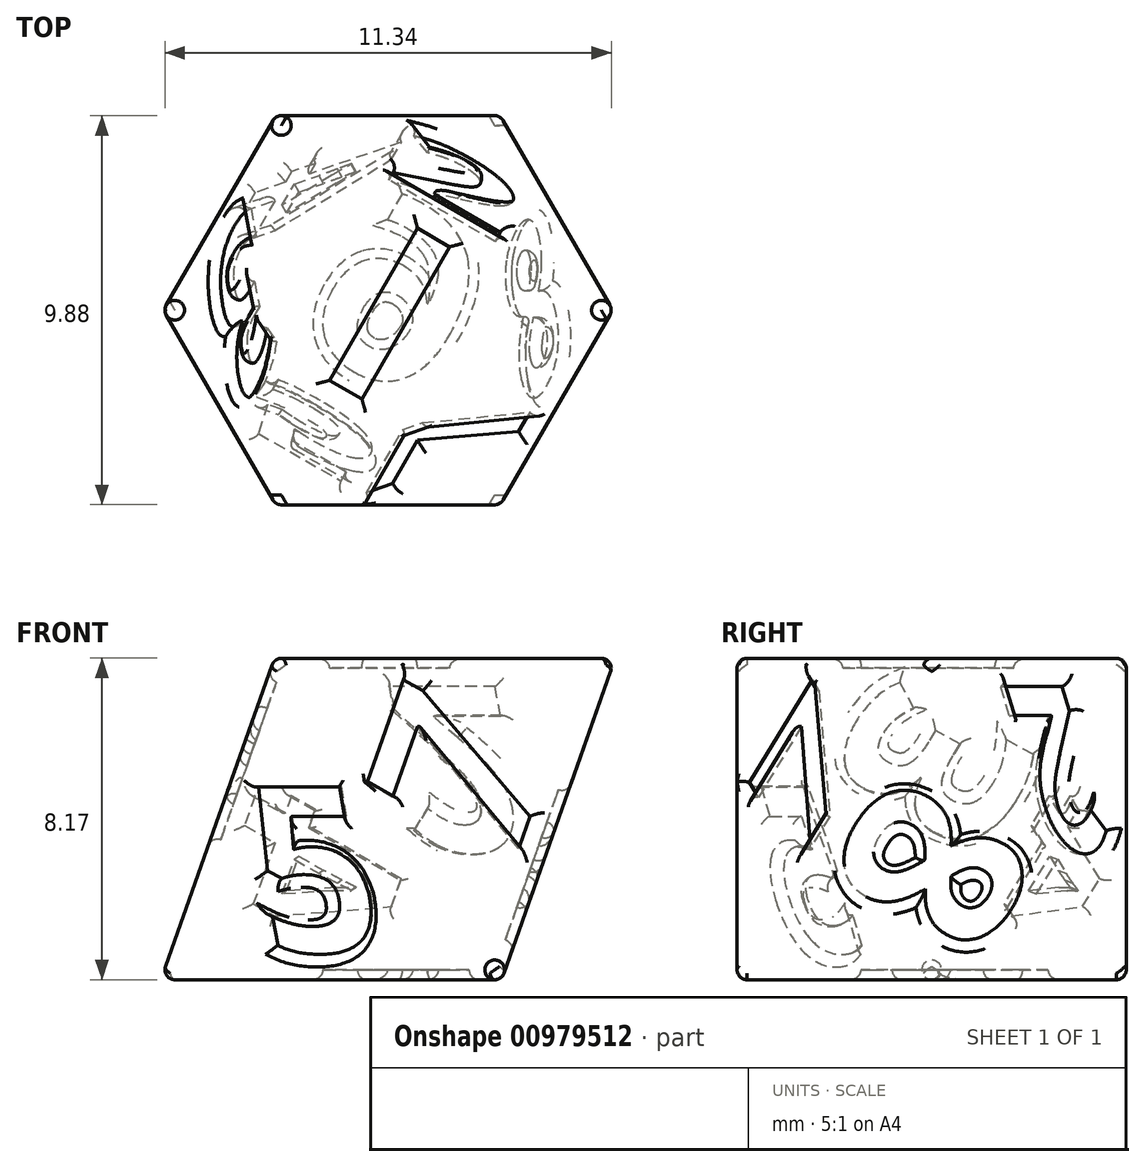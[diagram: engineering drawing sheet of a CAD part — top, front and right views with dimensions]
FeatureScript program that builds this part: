
annotation { "Feature Type Name" : "Feature", "Feature Type Description" : "" }
export const myFeature = defineFeature(function(context is Context, id is Id, definition is map)
    precondition{}
    {
        {
            var Q0;
            Q0=qCreatedBy(makeId("Top.planeOp"),FACE);
            var sketch = newSketch(context, id + "F0", { "sketchPlane" : qUnion([Q0])});
            skCircle(sketch, "E0.cCircle", {"center": v(0, 0) * mm, "radius": 2.89 * mm, "construction": true});
            skLineSegment(sketch, "E0.0", {"start": v(2.89, 5) * mm, "end": v(2.89, -5) * mm});
            skLineSegment(sketch, "E0.1", {"start": v(2.89, -5) * mm, "end": v(-5.77, 0) * mm});
            skLineSegment(sketch, "E0.2", {"start": v(-5.77, 0) * mm, "end": v(2.89, 5) * mm});
            skPoint(sketch, "E0.0.midPoint", {"position": v(2.89, 0) * mm});
            skSolve(sketch);
        }
        {
            var Q0;
            Q0=sQuery(id+"F0.wireOp",EDGE,"E0.2");
            cPlane(context, id + "F1", {"entities" : qUnion([Q0]), "cplaneType" : CPlaneType.LINE_ANGLE, "offset" : 25 * mm, "angle" : 199.47 * degree, "oppositeDirection" : true, "width" : 150 * mm, "height" : 150 * mm});
        }
        {
            var Q0;
            Q0=qCreatedBy(id+"F1.planeOp",FACE);
            var sketch = newSketch(context, id + "F2", { "sketchPlane" : qUnion([Q0])});
            skCircle(sketch, "E1.cCircle", {"center": v(-0.73, 3.78) * mm, "radius": 2.89 * mm, "construction": true});
            skLineSegment(sketch, "E1.0", {"start": v(4.73, 1.89) * mm, "end": v(-5.1, 0) * mm});
            skLineSegment(sketch, "E1.1", {"start": v(-5.1, 0) * mm, "end": v(-1.82, 9.45) * mm});
            skLineSegment(sketch, "E1.2", {"start": v(-1.82, 9.45) * mm, "end": v(4.73, 1.89) * mm});
            skPoint(sketch, "E1.0.midPoint", {"position": v(-0.18, 0.94) * mm});
            skSolve(sketch);
        }
        {
            var Q0;
            Q0=sQuery(id+"F0.wireOp",EDGE,"E0.0");
            cPlane(context, id + "F3", {"entities" : qUnion([Q0]), "cplaneType" : CPlaneType.LINE_ANGLE, "offset" : 25 * mm, "angle" : 109.47 * degree, "oppositeDirection" : true, "width" : 150 * mm, "height" : 150 * mm});
        }
        {
            var Q0;
            Q0=qCreatedBy(id+"F3.planeOp",FACE);
            var sketch = newSketch(context, id + "F4", { "sketchPlane" : qUnion([Q0])});
            skCircle(sketch, "E2.cCircle", {"center": v(0, 3.85) * mm, "radius": 2.89 * mm, "construction": true});
            skLineSegment(sketch, "E2.0", {"start": v(5, 0.96) * mm, "end": v(-5, 0.96) * mm});
            skLineSegment(sketch, "E2.1", {"start": v(-5, 0.96) * mm, "end": v(0, 9.62) * mm});
            skLineSegment(sketch, "E2.2", {"start": v(0, 9.62) * mm, "end": v(5, 0.96) * mm});
            skPoint(sketch, "E2.0.midPoint", {"position": v(0, 0.96) * mm});
            skSolve(sketch);
        }
        {
            var Q0;
            Q0=sQuery(id+"F0.wireOp",VERTEX,"E0.0.start");
            var Q1;
            Q1=sQuery(id+"F2.wireOp",VERTEX,"E1.1.end");
            var Q2;
            Q2=sQuery(id+"F4.wireOp",VERTEX,"E2.1.end");
            cPlane(context, id + "F5", {"entities" : qUnion([Q0, Q1, Q2]), "cplaneType" : CPlaneType.THREE_POINT, "offset" : 25 * mm, "width" : 150 * mm, "height" : 150 * mm});
        }
        {
            var Q0;
            Q0=qCreatedBy(id+"F5.planeOp",FACE);
            var sketch = newSketch(context, id + "F6", { "sketchPlane" : qUnion([Q0])});
            skPoint(sketch, "E3.0", {"position": v(3.64, 7.56) * mm});
            skPoint(sketch, "E4.0", {"position": v(-6.18, 5.67) * mm});
            skLineSegment(sketch, "E5", {"start": v(3.64, 7.56) * mm, "end": v(-6.18, 5.67) * mm});
            skPoint(sketch, "E6.0", {"position": v(0.36, -1.89) * mm});
            skLineSegment(sketch, "E7", {"start": v(3.64, 7.56) * mm, "end": v(0.36, -1.89) * mm});
            skLineSegment(sketch, "E8", {"start": v(-6.18, 5.67) * mm, "end": v(0.36, -1.89) * mm});
            skSolve(sketch);
        }
        {
            var Q0;
            Q0=sQuery(id+"F0.wireOp",EDGE,"E0.1");
            cPlane(context, id + "F7", {"entities" : qUnion([Q0]), "cplaneType" : CPlaneType.LINE_ANGLE, "offset" : 25 * mm, "angle" : 199.47 * degree, "oppositeDirection" : true, "width" : 150 * mm, "height" : 150 * mm});
        }
        {
            var Q0;
            Q0=qCreatedBy(id+"F7.planeOp",FACE);
            var sketch = newSketch(context, id + "F8", { "sketchPlane" : qUnion([Q0])});
            skCircle(sketch, "E9.cCircle", {"center": v(0.73, 3.78) * mm, "radius": 2.89 * mm, "construction": true});
            skLineSegment(sketch, "E9.0", {"start": v(5.1, 0) * mm, "end": v(-4.73, 1.89) * mm});
            skLineSegment(sketch, "E9.1", {"start": v(-4.73, 1.89) * mm, "end": v(1.82, 9.45) * mm});
            skLineSegment(sketch, "E9.2", {"start": v(1.82, 9.45) * mm, "end": v(5.1, 0) * mm});
            skPoint(sketch, "E9.0.midPoint", {"position": v(0.18, 0.94) * mm});
            skSolve(sketch);
        }
        {
            var Q0;
            Q0=sQuery(id+"F6.wireOp",VERTEX,"E4.0");
            var Q1;
            Q1=sQuery(id+"F8.wireOp",VERTEX,"E9.1.end");
            var Q2;
            Q2=sQuery(id+"F6.wireOp",VERTEX,"E3.0");
            cPlane(context, id + "F9", {"entities" : qUnion([Q0, Q1, Q2]), "cplaneType" : CPlaneType.THREE_POINT, "offset" : 25 * mm, "width" : 150 * mm, "height" : 150 * mm});
        }
        {
            var Q0;
            Q0=qCreatedBy(id+"F9.planeOp",FACE);
            var sketch = newSketch(context, id + "F10", { "sketchPlane" : qUnion([Q0])});
            skCircle(sketch, "E10.cCircle", {"center": v(0, 0) * mm, "radius": 2.89 * mm, "construction": true});
            skLineSegment(sketch, "E10.0", {"start": v(5.77, 0) * mm, "end": v(-2.89, -5) * mm});
            skLineSegment(sketch, "E10.1", {"start": v(-2.89, -5) * mm, "end": v(-2.89, 5) * mm});
            skLineSegment(sketch, "E10.2", {"start": v(-2.89, 5) * mm, "end": v(5.77, 0) * mm});
            skPoint(sketch, "E10.0.midPoint", {"position": v(1.44, -2.5) * mm});
            skSolve(sketch);
        }
        {
            var Q0;
            Q0=sQuery(id+"F6.wireOp",VERTEX,"E4.0");
            var Q1;
            Q1=sQuery(id+"F0.wireOp",VERTEX,"E0.1.end");
            var Q2;
            Q2=sQuery(id+"F8.wireOp",VERTEX,"E9.1.end");
            cPlane(context, id + "F11", {"entities" : qUnion([Q0, Q1, Q2]), "cplaneType" : CPlaneType.THREE_POINT, "offset" : 25 * mm, "width" : 150 * mm, "height" : 150 * mm});
        }
        {
            var Q0;
            Q0=qCreatedBy(id+"F11.planeOp",FACE);
            var sketch = newSketch(context, id + "F12", { "sketchPlane" : qUnion([Q0])});
            skCircle(sketch, "E11.cCircle", {"center": v(0, 3.85) * mm, "radius": 2.89 * mm, "construction": true});
            skLineSegment(sketch, "E11.0", {"start": v(0, -1.92) * mm, "end": v(-5, 6.74) * mm});
            skLineSegment(sketch, "E11.1", {"start": v(-5, 6.74) * mm, "end": v(5, 6.74) * mm});
            skLineSegment(sketch, "E11.2", {"start": v(5, 6.74) * mm, "end": v(0, -1.92) * mm});
            skPoint(sketch, "E11.0.midPoint", {"position": v(-2.5, 2.4) * mm});
            skSolve(sketch);
        }
        {
            var Q0;
            Q0=sQuery(id+"F0.wireOp",VERTEX,"E0.0.end");
            var Q1;
            Q1=sQuery(id+"F8.wireOp",VERTEX,"E9.1.end");
            var Q2;
            Q2=sQuery(id+"F6.wireOp",VERTEX,"E3.0");
            cPlane(context, id + "F13", {"entities" : qUnion([Q0, Q1, Q2]), "cplaneType" : CPlaneType.THREE_POINT, "offset" : 25 * mm, "width" : 150 * mm, "height" : 150 * mm});
        }
        {
            var Q0;
            Q0=qCreatedBy(id+"F13.planeOp",FACE);
            var sketch = newSketch(context, id + "F14", { "sketchPlane" : qUnion([Q0])});
            skCircle(sketch, "E12.cCircle", {"center": v(-0.73, 3.78) * mm, "radius": 2.89 * mm, "construction": true});
            skLineSegment(sketch, "E12.0", {"start": v(3.64, 7.56) * mm, "end": v(0.36, -1.89) * mm});
            skLineSegment(sketch, "E12.1", {"start": v(0.36, -1.89) * mm, "end": v(-6.18, 5.67) * mm});
            skLineSegment(sketch, "E12.2", {"start": v(-6.18, 5.67) * mm, "end": v(3.64, 7.56) * mm});
            skPoint(sketch, "E12.0.midPoint", {"position": v(2, 2.83) * mm});
            skSolve(sketch);
        }
        {
            var Q0;
            Q0=makeQuery(id+"F6.imprint","IMPRINT",FACE,{"disambiguationData":[TD([[makeQuery(id+"F6.imprint","IMPRINT",EDGE,{"derivedFrom":sQuery(id+"F6.wireOp",EDGE,"E5")}),1.0]])]});
            var Q1;
            Q1=makeQuery(id+"F8.imprint","IMPRINT",FACE,{"disambiguationData":[TD([[makeQuery(id+"F8.imprint","IMPRINT",EDGE,{"derivedFrom":sQuery(id+"F8.wireOp",EDGE,"E9.0")}),-1.0]])]});
            loft(context, id + "F15", {"sheetProfilesArray" : [{ "sheetProfileEntities" : qUnion([Q0]) }, { "sheetProfileEntities" : qUnion([Q1]) }]});
        }
        {
            var Q1;
            Q1=makeQuery(id+"F2.imprint","IMPRINT",FACE,{"disambiguationData":[TD([[makeQuery(id+"F2.imprint","IMPRINT",EDGE,{"derivedFrom":sQuery(id+"F2.wireOp",EDGE,"E1.0")}),-1.0]])]});
            var Q2;
            Q2=makeQuery(id+"F14.imprint","IMPRINT",FACE,{"disambiguationData":[TD([[makeQuery(id+"F14.imprint","IMPRINT",EDGE,{"derivedFrom":sQuery(id+"F14.wireOp",EDGE,"E12.0")}),-1.0]])]});
            loft(context, id + "F16", {"operationType" : NewBodyOperationType.ADD, "sheetProfilesArray" : [{ "sheetProfileEntities" : qUnion([Q1]) }, { "sheetProfileEntities" : qUnion([Q2]) }]});
        }
        {
            var Q1;
            Q1=makeQuery(id+"F10.imprint","IMPRINT",FACE,{"disambiguationData":[TD([[makeQuery(id+"F10.imprint","IMPRINT",EDGE,{"derivedFrom":sQuery(id+"F10.wireOp",EDGE,"E10.0")}),-1.0]])]});
            var Q2;
            Q2=makeQuery(id+"F0.imprint","IMPRINT",FACE,{"disambiguationData":[TD([[makeQuery(id+"F0.imprint","IMPRINT",EDGE,{"derivedFrom":sQuery(id+"F0.wireOp",EDGE,"E0.0")}),-1.0]])]});
            loft(context, id + "F17", {"operationType" : NewBodyOperationType.ADD, "sheetProfilesArray" : [{ "sheetProfileEntities" : qUnion([Q1]) }, { "sheetProfileEntities" : qUnion([Q2]) }]});
        }
        {
            var Q1;
            Q1=makeQuery(id+"F12.imprint","IMPRINT",FACE,{"disambiguationData":[TD([[makeQuery(id+"F12.imprint","IMPRINT",EDGE,{"derivedFrom":sQuery(id+"F12.wireOp",EDGE,"E11.0")}),-1.0]])]});
            var Q2;
            Q2=makeQuery(id+"F4.imprint","IMPRINT",FACE,{"disambiguationData":[TD([[makeQuery(id+"F4.imprint","IMPRINT",EDGE,{"derivedFrom":sQuery(id+"F4.wireOp",EDGE,"E2.0")}),-1.0]])]});
            loft(context, id + "F18", {"operationType" : NewBodyOperationType.ADD, "sheetProfilesArray" : [{ "sheetProfileEntities" : qUnion([Q1]) }, { "sheetProfileEntities" : qUnion([Q2]) }]});
        }
        {
            var Q0;
            Q0=makeQuery(id+"F17.opLoft","CAP_FACE",FACE,{"disambiguationData":[OSD([makeQuery(id+"F10.imprint","IMPRINT",FACE,{"disambiguationData":[TD([[makeQuery(id+"F10.imprint","IMPRINT",EDGE,{"derivedFrom":sQuery(id+"F10.wireOp",EDGE,"E10.0")}),-1.0]])]})])],"isStart":true});
            var sketch = newSketch(context, id + "F19", { "sketchPlane" : qUnion([Q0])});
            skText(sketch, "E13", { "text": "I", "fontName": "OpenSans-Bold.ttf"});
            skLineSegment(sketch, "E14", {"start": v(-2.89, -5) * mm, "end": v(-1.14, -1.97) * mm, "construction": true});
            const initialGuessF19  = {"E13": [-0.00197, -0.0015, 0.86603, -0.5, 0.0045]};
            skSetInitialGuess(sketch, initialGuessF19);
            skSolve(sketch);
        }
        {
            var Q0;
            Q0=makeQuery(id+"F19.imprint","IMPRINT",FACE,{"disambiguationData":[TD([[makeQuery(id+"F19.imprint","IMPRINT",EDGE,{"derivedFrom":sQuery(id+"F19.wireOp",EDGE,"E13.sketch_text.stroke-0")}),-1.0]])]});
            extrude(context, id + "F20", {"entities" : qUnion([Q0]), "operationType" : NewBodyOperationType.REMOVE, "oppositeDirection" : true, "depth" : .25 * mm, "offsetDistance" : 25 * mm});
        }
        {
            var Q0;
            Q0=makeQuery(id+"F18.opLoft","CAP_FACE",FACE,{"disambiguationData":[OSD([makeQuery(id+"F12.imprint","IMPRINT",FACE,{"disambiguationData":[TD([[makeQuery(id+"F12.imprint","IMPRINT",EDGE,{"derivedFrom":sQuery(id+"F12.wireOp",EDGE,"E11.0")}),-1.0]])]})])],"isStart":true});
            var sketch = newSketch(context, id + "F21", { "sketchPlane" : qUnion([Q0])});
            skText(sketch, "E15", { "text": "3", "fontName": "OpenSans-Bold.ttf"});
            skLineSegment(sketch, "E16", {"start": v(5, 6.74) * mm, "end": v(1.97, 4.99) * mm, "construction": true});
            skPoint(sketch, "E17.0", {"position": v(-2.5, 2.4) * mm});
            skLineSegment(sketch, "E18", {"start": v(-2.5, 2.4) * mm, "end": v(-1.93, 2.74) * mm, "construction": true});
            skFitSpline(sketch, "E19.0", {"points": [v(-5, 6.74) * mm, v(0, -1.92) * mm]});
            const initialGuessF21  = {"E15": [-0.00286, 0.00435, 0.49999, -0.86603, 0.0045]};
            skSetInitialGuess(sketch, initialGuessF21);
            skSolve(sketch);
        }
        {
            var Q0;
            Q0=makeQuery(id+"F21.imprint","IMPRINT",FACE,{"disambiguationData":[TD([[makeQuery(id+"F21.imprint","IMPRINT",EDGE,{"derivedFrom":sQuery(id+"F21.wireOp",EDGE,"E15.sketch_text.stroke-0")}),-1.0]])]});
            extrude(context, id + "F22", {"entities" : qUnion([Q0]), "operationType" : NewBodyOperationType.REMOVE, "oppositeDirection" : true, "depth" : .25 * mm, "offsetDistance" : 25 * mm});
        }
        {
            var Q0;
            Q0=makeQuery(id+"F15.opLoft","CAP_FACE",FACE,{"disambiguationData":[OSD([makeQuery(id+"F8.imprint","IMPRINT",FACE,{"disambiguationData":[TD([[makeQuery(id+"F8.imprint","IMPRINT",EDGE,{"derivedFrom":sQuery(id+"F8.wireOp",EDGE,"E9.0")}),-1.0]])]})])],"isStart":true});
            var sketch = newSketch(context, id + "F23", { "sketchPlane" : qUnion([Q0])});
            skLineSegment(sketch, "E20", {"start": v(-0.18, 0.94) * mm, "end": v(-0.3, 1.6) * mm, "construction": true});
            skLineSegment(sketch, "E21", {"start": v(-1.82, 9.45) * mm, "end": v(-1.16, 6.01) * mm, "construction": true});
            skText(sketch, "E22", { "text": "5", "fontName": "OpenSans-Bold.ttf"});
            const initialGuessF23  = {"E22": [-0.00212, 0.00124, 0.98198, 0.18897, 0.0045]};
            skSetInitialGuess(sketch, initialGuessF23);
            skSolve(sketch);
        }
        {
            var Q0;
            Q0=makeQuery(id+"F23.imprint","IMPRINT",FACE,{"disambiguationData":[TD([[makeQuery(id+"F23.imprint","IMPRINT",EDGE,{"derivedFrom":sQuery(id+"F23.wireOp",EDGE,"E22.sketch_text.stroke-0")}),-1.0]])]});
            extrude(context, id + "F24", {"entities" : qUnion([Q0]), "operationType" : NewBodyOperationType.REMOVE, "oppositeDirection" : true, "depth" : .25 * mm, "offsetDistance" : 25 * mm});
        }
        {
            var Q0;
            Q0=makeQuery(id+"F16.opLoft","CAP_FACE",FACE,{"disambiguationData":[OSD([makeQuery(id+"F14.imprint","IMPRINT",FACE,{"disambiguationData":[TD([[makeQuery(id+"F14.imprint","IMPRINT",EDGE,{"derivedFrom":sQuery(id+"F14.wireOp",EDGE,"E12.0")}),-1.0]])]})])],"isStart":true});
            var sketch = newSketch(context, id + "F25", { "sketchPlane" : qUnion([Q0])});
            skLineSegment(sketch, "E23", {"start": v(2, 2.83) * mm, "end": v(1.38, 3.05) * mm, "construction": true});
            skLineSegment(sketch, "E24", {"start": v(-6.18, 5.67) * mm, "end": v(-2.88, 4.52) * mm, "construction": true});
            skText(sketch, "E25", { "text": "7", "fontName": "OpenSans-Bold.ttf"});
            const initialGuessF25  = {"E25": [0.00076, 0.00127, 0.32732, 0.94491, 0.0045]};
            skSetInitialGuess(sketch, initialGuessF25);
            skSolve(sketch);
        }
        {
            var Q0;
            Q0=makeQuery(id+"F25.imprint","IMPRINT",FACE,{"disambiguationData":[TD([[makeQuery(id+"F25.imprint","IMPRINT",EDGE,{"derivedFrom":sQuery(id+"F25.wireOp",EDGE,"E25.sketch_text.stroke-0")}),-1.0]])]});
            extrude(context, id + "F26", {"entities" : qUnion([Q0]), "operationType" : NewBodyOperationType.REMOVE, "oppositeDirection" : true, "depth" : .25 * mm, "offsetDistance" : 25 * mm});
        }
        {
            var Q0;
            Q0=makeQuery(id+"F17.opLoft","CAP_FACE",FACE,{"disambiguationData":[OSD([makeQuery(id+"F0.imprint","IMPRINT",FACE,{"disambiguationData":[TD([[makeQuery(id+"F0.imprint","IMPRINT",EDGE,{"derivedFrom":sQuery(id+"F0.wireOp",EDGE,"E0.0")}),-1.0]])]})])],"isStart":true});
            var sketch = newSketch(context, id + "F27", { "sketchPlane" : qUnion([Q0])});
            skLineSegment(sketch, "E26", {"start": v(-1.44, 2.5) * mm, "end": v(-0.86, 1.5) * mm, "construction": true});
            skLineSegment(sketch, "E27", {"start": v(2.89, -5) * mm, "end": v(1.39, -2.4) * mm, "construction": true});
            skText(sketch, "E28", { "text": "6", "fontName": "OpenSans-Bold.ttf"});
            const initialGuessF27  = {"E28": [0.00077, 0.00244, -0.86603, -0.5, 0.0045]};
            skSetInitialGuess(sketch, initialGuessF27);
            skSolve(sketch);
        }
        {
            var Q0;
            Q0=makeQuery(id+"F27.imprint","IMPRINT",FACE,{"disambiguationData":[TD([[makeQuery(id+"F27.imprint","IMPRINT",EDGE,{"derivedFrom":sQuery(id+"F27.wireOp",EDGE,"E28.sketch_text.stroke-0")}),-1.0]])]});
            extrude(context, id + "F28", {"entities" : qUnion([Q0]), "operationType" : NewBodyOperationType.REMOVE, "oppositeDirection" : true, "depth" : .25 * mm, "offsetDistance" : 25 * mm});
        }
        {
            var Q0;
            Q0=makeQuery(id+"F16.opLoft","CAP_FACE",FACE,{"disambiguationData":[OSD([makeQuery(id+"F2.imprint","IMPRINT",FACE,{"disambiguationData":[TD([[makeQuery(id+"F2.imprint","IMPRINT",EDGE,{"derivedFrom":sQuery(id+"F2.wireOp",EDGE,"E1.0")}),-1.0]])]})])],"isStart":true});
            var sketch = newSketch(context, id + "F29", { "sketchPlane" : qUnion([Q0])});
            skText(sketch, "E29", { "text": "4", "fontName": "OpenSans-Bold.ttf"});
            skLineSegment(sketch, "E30", {"start": v(-4.73, 1.89) * mm, "end": v(-1.42, 3.04) * mm, "construction": true});
            skPoint(sketch, "E31.0", {"position": v(3.46, 4.72) * mm});
            skLineSegment(sketch, "E32", {"start": v(3.46, 4.72) * mm, "end": v(2.83, 4.5) * mm, "construction": true});
            const initialGuessF29  = {"E29": [0.00347, 0.00268, -0.32734, 0.9449, 0.0045]};
            skSetInitialGuess(sketch, initialGuessF29);
            skSolve(sketch);
        }
        {
            var Q0;
            Q0=makeQuery(id+"F29.imprint","IMPRINT",FACE,{"disambiguationData":[TD([[makeQuery(id+"F29.imprint","IMPRINT",EDGE,{"derivedFrom":sQuery(id+"F29.wireOp",EDGE,"E29.sketch_text.stroke-0")}),-1.0]])]});
            extrude(context, id + "F30", {"entities" : qUnion([Q0]), "operationType" : NewBodyOperationType.REMOVE, "oppositeDirection" : true, "depth" : .25 * mm, "offsetDistance" : 25 * mm});
        }
        {
            var Q0;
            Q0=makeQuery(id+"F15.opLoft","CAP_FACE",FACE,{"disambiguationData":[OSD([makeQuery(id+"F6.imprint","IMPRINT",FACE,{"disambiguationData":[TD([[makeQuery(id+"F6.imprint","IMPRINT",EDGE,{"derivedFrom":sQuery(id+"F6.wireOp",EDGE,"E5")}),1.0]])]})])],"isStart":true});
            var sketch = newSketch(context, id + "F31", { "sketchPlane" : qUnion([Q0])});
            skText(sketch, "E33", { "text": "2", "fontName": "OpenSans-Bold.ttf"});
            skLineSegment(sketch, "E34", {"start": v(-0.36, -1.89) * mm, "end": v(0.3, 1.55) * mm, "construction": true});
            skPoint(sketch, "E35.0", {"position": v(1.27, 6.61) * mm});
            skLineSegment(sketch, "E36", {"start": v(1.27, 6.61) * mm, "end": v(1.15, 5.97) * mm, "construction": true});
            const initialGuessF31  = {"E33": [0.003, 0.0056, -0.98198, 0.18899, 0.0045]};
            skSetInitialGuess(sketch, initialGuessF31);
            skSolve(sketch);
        }
        {
            var Q0;
            Q0=makeQuery(id+"F31.imprint","IMPRINT",FACE,{"disambiguationData":[TD([[makeQuery(id+"F31.imprint","IMPRINT",EDGE,{"derivedFrom":sQuery(id+"F31.wireOp",EDGE,"E33.sketch_text.stroke-0")}),-1.0]])]});
            extrude(context, id + "F32", {"entities" : qUnion([Q0]), "operationType" : NewBodyOperationType.REMOVE, "oppositeDirection" : true, "depth" : .25 * mm, "offsetDistance" : 25 * mm});
        }
        {
            var Q0;
            Q0=makeQuery(id+"F18.opLoft","CAP_FACE",FACE,{"disambiguationData":[OSD([makeQuery(id+"F4.imprint","IMPRINT",FACE,{"disambiguationData":[TD([[makeQuery(id+"F4.imprint","IMPRINT",EDGE,{"derivedFrom":sQuery(id+"F4.wireOp",EDGE,"E2.0")}),-1.0]])]})])],"isStart":true});
            var sketch = newSketch(context, id + "F33", { "sketchPlane" : qUnion([Q0])});
            skText(sketch, "E37", { "text": "8", "fontName": "OpenSans-Bold.ttf"});
            skPoint(sketch, "E38", {"position": v(-2.5, 5.3) * mm});
            skLineSegment(sketch, "E39", {"start": v(-2.5, 5.3) * mm, "end": v(-1.93, 4.96) * mm, "construction": true});
            skLineSegment(sketch, "E40", {"start": v(5, 0.96) * mm, "end": v(1.97, 2.71) * mm, "construction": true});
            const initialGuessF33  = {"E37": [-0.00099, 0.00659, -0.5, -0.86603, 0.0045]};
            skSetInitialGuess(sketch, initialGuessF33);
            skSolve(sketch);
        }
        {
            var Q0;
            Q0=makeQuery(id+"F33.imprint","IMPRINT",FACE,{"disambiguationData":[TD([[makeQuery(id+"F33.imprint","IMPRINT",EDGE,{"derivedFrom":sQuery(id+"F33.wireOp",EDGE,"E37.sketch_text.stroke-0")}),-1.0]])]});
            extrude(context, id + "F34", {"entities" : qUnion([Q0]), "operationType" : NewBodyOperationType.REMOVE, "oppositeDirection" : true, "depth" : .25 * mm, "offsetDistance" : 25 * mm});
        }
        {
            var Q0;
            {var subQ0=sQuery(id+"F10.wireOp",EDGE,"E10.2");var subQ1=sQuery(id+"F10.wireOp",EDGE,"E10.1");var subQ2=sQuery(id+"F10.wireOp",EDGE,"E10.0");var subQ3=sQuery(id+"F14.wireOp",EDGE,"E12.2");var subQ4=sQuery(id+"F14.wireOp",EDGE,"E12.1");var subQ5=sQuery(id+"F14.wireOp",EDGE,"E12.0");Q0=makeQuery(id+"F17.boolean.opBoolean","MERGE",EDGE,{"derivedFrom":[makeQuery(id+"F16.boolean.opBoolean","MERGE",EDGE,{"derivedFrom":[makeQuery(id+"F15.opLoft","SWEPT_EDGE",EDGE,{"disambiguationData":[OSD([sQuery(id+"F6.wireOp",EDGE,"E5"),sQuery(id+"F6.wireOp",EDGE,"E7"),sQuery(id+"F8.wireOp",EDGE,"E9.1"),sQuery(id+"F8.wireOp",EDGE,"E9.2")])]}),makeQuery(id+"F16.opLoft","MID_CAP_EDGE",EDGE,{"disambiguationData":[OSD([subQ5,subQ4,subQ3]),TDD([makeQuery(id+"F14.imprint","INTERSECT",VERTEX,{"derivedFrom":[subQ5,subQ3]}),makeQuery(id+"F14.imprint","INTERSECT",VERTEX,{"derivedFrom":[subQ4,subQ3]}),makeQuery(id+"F14.imprint","IMPRINT",EDGE,{"derivedFrom":subQ3})])],"capPos":1.0})]}),makeQuery(id+"F17.opLoft","MID_CAP_EDGE",EDGE,{"disambiguationData":[OSD([subQ2,subQ1,subQ0]),TDD([makeQuery(id+"F10.imprint","INTERSECT",VERTEX,{"derivedFrom":[subQ2,subQ0]}),makeQuery(id+"F10.imprint","INTERSECT",VERTEX,{"derivedFrom":[subQ1,subQ0]}),makeQuery(id+"F10.imprint","IMPRINT",EDGE,{"derivedFrom":subQ0})])],"capPos":0.0})]});}
            var Q1;
            {var subQ0=sQuery(id+"F12.wireOp",EDGE,"E11.1");var subQ1=sQuery(id+"F12.wireOp",EDGE,"E11.2");var subQ2=sQuery(id+"F12.wireOp",EDGE,"E11.0");var subQ3=sQuery(id+"F10.wireOp",EDGE,"E10.1");var subQ4=sQuery(id+"F10.wireOp",EDGE,"E10.2");var subQ5=sQuery(id+"F10.wireOp",EDGE,"E10.0");Q1=makeQuery(id+"F18.boolean.opBoolean","MERGE",EDGE,{"derivedFrom":[makeQuery(id+"F17.opLoft","MID_CAP_EDGE",EDGE,{"disambiguationData":[OSD([subQ5,subQ3,subQ4]),TDD([makeQuery(id+"F10.imprint","INTERSECT",VERTEX,{"derivedFrom":[subQ5,subQ3]}),makeQuery(id+"F10.imprint","INTERSECT",VERTEX,{"derivedFrom":[subQ3,subQ4]}),makeQuery(id+"F10.imprint","IMPRINT",EDGE,{"derivedFrom":subQ3})])],"capPos":0.0}),makeQuery(id+"F18.opLoft","MID_CAP_EDGE",EDGE,{"disambiguationData":[OSD([subQ2,subQ0,subQ1]),TDD([makeQuery(id+"F12.imprint","INTERSECT",VERTEX,{"derivedFrom":[subQ2,subQ0]}),makeQuery(id+"F12.imprint","INTERSECT",VERTEX,{"derivedFrom":[subQ0,subQ1]}),makeQuery(id+"F12.imprint","IMPRINT",EDGE,{"derivedFrom":subQ0})])],"capPos":0.0})]});}
            var Q2;
            {var subQ0=sQuery(id+"F14.wireOp",EDGE,"E12.1");var subQ1=sQuery(id+"F14.wireOp",EDGE,"E12.2");var subQ2=sQuery(id+"F14.wireOp",EDGE,"E12.0");var subQ3=sQuery(id+"F8.wireOp",EDGE,"E9.1");var subQ4=sQuery(id+"F8.wireOp",EDGE,"E9.2");var subQ5=sQuery(id+"F8.wireOp",EDGE,"E9.0");Q2=makeQuery(id+"F16.boolean.opBoolean","MERGE",EDGE,{"derivedFrom":[makeQuery(id+"F15.opLoft","MID_CAP_EDGE",EDGE,{"disambiguationData":[OSD([subQ5,subQ3,subQ4]),TDD([makeQuery(id+"F8.imprint","INTERSECT",VERTEX,{"derivedFrom":[subQ5,subQ3]}),makeQuery(id+"F8.imprint","INTERSECT",VERTEX,{"derivedFrom":[subQ3,subQ4]}),makeQuery(id+"F8.imprint","IMPRINT",EDGE,{"derivedFrom":subQ3})])],"capPos":1.0}),makeQuery(id+"F16.opLoft","MID_CAP_EDGE",EDGE,{"disambiguationData":[OSD([subQ2,subQ0,subQ1]),TDD([makeQuery(id+"F14.imprint","INTERSECT",VERTEX,{"derivedFrom":[subQ2,subQ0]}),makeQuery(id+"F14.imprint","INTERSECT",VERTEX,{"derivedFrom":[subQ0,subQ1]}),makeQuery(id+"F14.imprint","IMPRINT",EDGE,{"derivedFrom":subQ0})])],"capPos":1.0})]});}
            var Q3;
            {var subQ0=sQuery(id+"F12.wireOp",EDGE,"E11.0");var subQ1=sQuery(id+"F12.wireOp",EDGE,"E11.1");var subQ2=sQuery(id+"F12.wireOp",EDGE,"E11.2");var subQ3=sQuery(id+"F8.wireOp",EDGE,"E9.2");var subQ4=sQuery(id+"F8.wireOp",EDGE,"E9.1");var subQ5=sQuery(id+"F8.wireOp",EDGE,"E9.0");Q3=makeQuery(id+"F18.boolean.opBoolean","MERGE",EDGE,{"derivedFrom":[makeQuery(id+"F15.opLoft","MID_CAP_EDGE",EDGE,{"disambiguationData":[OSD([subQ5,subQ4,subQ3]),TDD([makeQuery(id+"F8.imprint","INTERSECT",VERTEX,{"derivedFrom":[subQ5,subQ3]}),makeQuery(id+"F8.imprint","INTERSECT",VERTEX,{"derivedFrom":[subQ4,subQ3]}),makeQuery(id+"F8.imprint","IMPRINT",EDGE,{"derivedFrom":subQ3})])],"capPos":1.0}),makeQuery(id+"F18.opLoft","MID_CAP_EDGE",EDGE,{"disambiguationData":[OSD([subQ0,subQ1,subQ2]),TDD([makeQuery(id+"F12.imprint","INTERSECT",VERTEX,{"derivedFrom":[subQ0,subQ2]}),makeQuery(id+"F12.imprint","INTERSECT",VERTEX,{"derivedFrom":[subQ0,subQ1]}),makeQuery(id+"F12.imprint","IMPRINT",EDGE,{"derivedFrom":subQ0})])],"capPos":0.0})]});}
            var Q4;
            {var subQ0=sQuery(id+"F4.wireOp",EDGE,"E2.1");var subQ1=sQuery(id+"F4.wireOp",EDGE,"E2.2");var subQ2=sQuery(id+"F4.wireOp",EDGE,"E2.0");var subQ3=sQuery(id+"F6.wireOp",EDGE,"E7");var subQ4=sQuery(id+"F6.wireOp",EDGE,"E8");var subQ5=sQuery(id+"F6.wireOp",EDGE,"E5");Q4=makeQuery(id+"F18.boolean.opBoolean","MERGE",EDGE,{"derivedFrom":[makeQuery(id+"F15.opLoft","MID_CAP_EDGE",EDGE,{"disambiguationData":[OSD([subQ5,subQ3,subQ4]),TDD([makeQuery(id+"F6.imprint","INTERSECT",VERTEX,{"derivedFrom":[subQ5,subQ3]}),makeQuery(id+"F6.imprint","INTERSECT",VERTEX,{"derivedFrom":[subQ3,subQ4]}),makeQuery(id+"F6.imprint","IMPRINT",EDGE,{"derivedFrom":subQ3})])],"capPos":0.0}),makeQuery(id+"F18.opLoft","MID_CAP_EDGE",EDGE,{"disambiguationData":[OSD([subQ2,subQ0,subQ1]),TDD([makeQuery(id+"F4.imprint","INTERSECT",VERTEX,{"derivedFrom":[subQ2,subQ0]}),makeQuery(id+"F4.imprint","INTERSECT",VERTEX,{"derivedFrom":[subQ0,subQ1]}),makeQuery(id+"F4.imprint","IMPRINT",EDGE,{"derivedFrom":subQ0})])],"capPos":1.0})]});}
            var Q5;
            {var subQ0=sQuery(id+"F4.wireOp",EDGE,"E2.0");var subQ1=sQuery(id+"F4.wireOp",EDGE,"E2.1");var subQ2=sQuery(id+"F4.wireOp",EDGE,"E2.2");var subQ3=sQuery(id+"F0.wireOp",EDGE,"E0.0");var subQ4=sQuery(id+"F0.wireOp",EDGE,"E0.1");var subQ5=sQuery(id+"F0.wireOp",EDGE,"E0.2");var subQ6=makeQuery(id+"F17.opLoft","MID_CAP_EDGE",EDGE,{"disambiguationData":[OSD([subQ3,subQ4,subQ5]),TDD([makeQuery(id+"F0.imprint","INTERSECT",VERTEX,{"derivedFrom":[subQ3,subQ5]}),makeQuery(id+"F0.imprint","INTERSECT",VERTEX,{"derivedFrom":[subQ3,subQ4]}),makeQuery(id+"F0.imprint","IMPRINT",EDGE,{"derivedFrom":subQ3})])],"capPos":1.0});var subQ7=sQuery(id+"F8.wireOp",EDGE,"E9.1");var subQ8=sQuery(id+"F8.wireOp",EDGE,"E9.2");var subQ9=sQuery(id+"F8.wireOp",EDGE,"E9.0");var subQ10=makeQuery(id+"F8.imprint","INTERSECT",VERTEX,{"derivedFrom":[subQ9,subQ7]});var subQ11=sQuery(id+"F6.wireOp",EDGE,"E7");var subQ12=sQuery(id+"F6.wireOp",EDGE,"E8");var subQ13=makeQuery(id+"F6.imprint","INTERSECT",VERTEX,{"derivedFrom":[subQ11,subQ12]});var subQ14=sQuery(id+"F6.wireOp",EDGE,"E5");var subQ15=sQuery(id+"F14.wireOp",EDGE,"E12.1");var subQ17=sQuery(id+"F14.wireOp",EDGE,"E12.0");var subQ19=sQuery(id+"F2.wireOp",EDGE,"E1.0");var subQ21=sQuery(id+"F2.wireOp",EDGE,"E1.2");var subQ23=makeQuery(id+"F16.opLoft","SWEPT_EDGE",EDGE,{"disambiguationData":[OSD([subQ19,subQ21,subQ17,subQ15])]});var subQ24=makeQuery(id+"F15.opLoft","SWEPT_EDGE",EDGE,{"disambiguationData":[OSD([subQ11,subQ12,subQ9,subQ7])]});Q5=makeQuery(id+"F18.boolean.opBoolean","MERGE",EDGE,{"derivedFrom":[makeQuery(id+"F17.boolean.opBoolean","MERGE",EDGE,{"derivedFrom":[makeQuery(id+"F16.boolean.opBoolean","SPLIT",EDGE,{"derivedFrom":subQ23}),makeQuery(id+"F16.boolean.opBoolean","MERGE",EDGE,{"disambiguationData":[topologyDisambiguationEdgeConnected([makeQuery(id+"F15.opLoft","SWEPT_FACE",FACE,{"disambiguationData":[OSD([subQ14,subQ11,subQ12,subQ9,subQ7,subQ8]),TDD([makeQuery(id+"F6.imprint","INTERSECT",VERTEX,{"derivedFrom":[subQ14,subQ12]}),subQ13,makeQuery(id+"F6.imprint","IMPRINT",EDGE,{"derivedFrom":subQ12}),makeQuery(id+"F8.imprint","INTERSECT",VERTEX,{"derivedFrom":[subQ9,subQ8]}),subQ10,makeQuery(id+"F8.imprint","IMPRINT",EDGE,{"derivedFrom":subQ9})])]})])],"derivedFrom":[subQ24,subQ23]}),subQ6]}),makeQuery(id+"F17.boolean.opBoolean","MERGE",EDGE,{"derivedFrom":[makeQuery(id+"F16.boolean.opBoolean","MERGE",EDGE,{"disambiguationData":[topologyDisambiguationEdgeConnected([makeQuery(id+"F15.opLoft","SWEPT_FACE",FACE,{"disambiguationData":[OSD([subQ14,subQ11,subQ12,subQ9,subQ7,subQ8]),TDD([makeQuery(id+"F6.imprint","INTERSECT",VERTEX,{"derivedFrom":[subQ14,subQ11]}),subQ13,makeQuery(id+"F6.imprint","IMPRINT",EDGE,{"derivedFrom":subQ11}),subQ10,makeQuery(id+"F8.imprint","INTERSECT",VERTEX,{"derivedFrom":[subQ7,subQ8]}),makeQuery(id+"F8.imprint","IMPRINT",EDGE,{"derivedFrom":subQ7})])]})])],"derivedFrom":[subQ24,subQ23]}),subQ6]}),makeQuery(id+"F18.opLoft","MID_CAP_EDGE",EDGE,{"disambiguationData":[OSD([subQ0,subQ1,subQ2]),TDD([makeQuery(id+"F4.imprint","INTERSECT",VERTEX,{"derivedFrom":[subQ0,subQ2]}),makeQuery(id+"F4.imprint","INTERSECT",VERTEX,{"derivedFrom":[subQ0,subQ1]}),makeQuery(id+"F4.imprint","IMPRINT",EDGE,{"derivedFrom":subQ0})])],"capPos":1.0})]});}
            var Q6;
            {var subQ0=sQuery(id+"F0.wireOp",EDGE,"E0.2");var subQ1=sQuery(id+"F0.wireOp",EDGE,"E0.1");var subQ2=sQuery(id+"F0.wireOp",EDGE,"E0.0");var subQ3=sQuery(id+"F2.wireOp",EDGE,"E1.0");var subQ4=sQuery(id+"F2.wireOp",EDGE,"E1.1");var subQ5=sQuery(id+"F2.wireOp",EDGE,"E1.2");Q6=makeQuery(id+"F17.boolean.opBoolean","MERGE",EDGE,{"derivedFrom":[makeQuery(id+"F16.opLoft","MID_CAP_EDGE",EDGE,{"disambiguationData":[OSD([subQ3,subQ4,subQ5]),TDD([makeQuery(id+"F2.imprint","INTERSECT",VERTEX,{"derivedFrom":[subQ3,subQ5]}),makeQuery(id+"F2.imprint","INTERSECT",VERTEX,{"derivedFrom":[subQ3,subQ4]}),makeQuery(id+"F2.imprint","IMPRINT",EDGE,{"derivedFrom":subQ3})])],"capPos":0.0}),makeQuery(id+"F17.opLoft","MID_CAP_EDGE",EDGE,{"disambiguationData":[OSD([subQ2,subQ1,subQ0]),TDD([makeQuery(id+"F0.imprint","INTERSECT",VERTEX,{"derivedFrom":[subQ2,subQ0]}),makeQuery(id+"F0.imprint","INTERSECT",VERTEX,{"derivedFrom":[subQ1,subQ0]}),makeQuery(id+"F0.imprint","IMPRINT",EDGE,{"derivedFrom":subQ0})])],"capPos":1.0})]});}
            var Q7;
            {var subQ0=sQuery(id+"F2.wireOp",EDGE,"E1.2");var subQ1=sQuery(id+"F2.wireOp",EDGE,"E1.1");var subQ2=sQuery(id+"F2.wireOp",EDGE,"E1.0");var subQ3=sQuery(id+"F6.wireOp",EDGE,"E8");var subQ4=sQuery(id+"F6.wireOp",EDGE,"E7");var subQ5=sQuery(id+"F6.wireOp",EDGE,"E5");Q7=makeQuery(id+"F16.boolean.opBoolean","MERGE",EDGE,{"derivedFrom":[makeQuery(id+"F15.opLoft","MID_CAP_EDGE",EDGE,{"disambiguationData":[OSD([subQ5,subQ4,subQ3]),TDD([makeQuery(id+"F6.imprint","INTERSECT",VERTEX,{"derivedFrom":[subQ5,subQ3]}),makeQuery(id+"F6.imprint","INTERSECT",VERTEX,{"derivedFrom":[subQ4,subQ3]}),makeQuery(id+"F6.imprint","IMPRINT",EDGE,{"derivedFrom":subQ3})])],"capPos":0.0}),makeQuery(id+"F16.opLoft","MID_CAP_EDGE",EDGE,{"disambiguationData":[OSD([subQ2,subQ1,subQ0]),TDD([makeQuery(id+"F2.imprint","INTERSECT",VERTEX,{"derivedFrom":[subQ2,subQ0]}),makeQuery(id+"F2.imprint","INTERSECT",VERTEX,{"derivedFrom":[subQ1,subQ0]}),makeQuery(id+"F2.imprint","IMPRINT",EDGE,{"derivedFrom":subQ0})])],"capPos":0.0})]});}
            var Q8;
            {var subQ0=sQuery(id+"F0.wireOp",EDGE,"E0.1");var subQ1=sQuery(id+"F0.wireOp",EDGE,"E0.2");var subQ2=sQuery(id+"F0.wireOp",EDGE,"E0.0");var subQ3=sQuery(id+"F8.wireOp",EDGE,"E9.0");var subQ4=sQuery(id+"F8.wireOp",EDGE,"E9.1");var subQ5=sQuery(id+"F8.wireOp",EDGE,"E9.2");Q8=makeQuery(id+"F17.boolean.opBoolean","MERGE",EDGE,{"derivedFrom":[makeQuery(id+"F15.opLoft","MID_CAP_EDGE",EDGE,{"disambiguationData":[OSD([subQ3,subQ4,subQ5]),TDD([makeQuery(id+"F8.imprint","INTERSECT",VERTEX,{"derivedFrom":[subQ3,subQ5]}),makeQuery(id+"F8.imprint","INTERSECT",VERTEX,{"derivedFrom":[subQ3,subQ4]}),makeQuery(id+"F8.imprint","IMPRINT",EDGE,{"derivedFrom":subQ3})])],"capPos":1.0}),makeQuery(id+"F17.opLoft","MID_CAP_EDGE",EDGE,{"disambiguationData":[OSD([subQ2,subQ0,subQ1]),TDD([makeQuery(id+"F0.imprint","INTERSECT",VERTEX,{"derivedFrom":[subQ2,subQ0]}),makeQuery(id+"F0.imprint","INTERSECT",VERTEX,{"derivedFrom":[subQ0,subQ1]}),makeQuery(id+"F0.imprint","IMPRINT",EDGE,{"derivedFrom":subQ0})])],"capPos":1.0})]});}
            var Q9;
            {var subQ0=sQuery(id+"F4.wireOp",EDGE,"E2.2");var subQ1=sQuery(id+"F4.wireOp",EDGE,"E2.1");var subQ2=sQuery(id+"F4.wireOp",EDGE,"E2.0");var subQ3=sQuery(id+"F14.wireOp",EDGE,"E12.0");var subQ4=sQuery(id+"F14.wireOp",EDGE,"E12.1");var subQ5=sQuery(id+"F14.wireOp",EDGE,"E12.2");Q9=makeQuery(id+"F18.boolean.opBoolean","MERGE",EDGE,{"derivedFrom":[makeQuery(id+"F16.opLoft","MID_CAP_EDGE",EDGE,{"disambiguationData":[OSD([subQ3,subQ4,subQ5]),TDD([makeQuery(id+"F14.imprint","INTERSECT",VERTEX,{"derivedFrom":[subQ3,subQ5]}),makeQuery(id+"F14.imprint","INTERSECT",VERTEX,{"derivedFrom":[subQ3,subQ4]}),makeQuery(id+"F14.imprint","IMPRINT",EDGE,{"derivedFrom":subQ3})])],"capPos":1.0}),makeQuery(id+"F18.opLoft","MID_CAP_EDGE",EDGE,{"disambiguationData":[OSD([subQ2,subQ1,subQ0]),TDD([makeQuery(id+"F4.imprint","INTERSECT",VERTEX,{"derivedFrom":[subQ2,subQ0]}),makeQuery(id+"F4.imprint","INTERSECT",VERTEX,{"derivedFrom":[subQ1,subQ0]}),makeQuery(id+"F4.imprint","IMPRINT",EDGE,{"derivedFrom":subQ0})])],"capPos":1.0})]});}
            var Q10;
            {var subQ0=sQuery(id+"F10.wireOp",EDGE,"E10.0");var subQ1=sQuery(id+"F10.wireOp",EDGE,"E10.1");var subQ2=sQuery(id+"F10.wireOp",EDGE,"E10.2");var subQ3=sQuery(id+"F6.wireOp",EDGE,"E5");var subQ4=sQuery(id+"F6.wireOp",EDGE,"E8");var subQ5=sQuery(id+"F6.wireOp",EDGE,"E7");Q10=makeQuery(id+"F17.boolean.opBoolean","MERGE",EDGE,{"derivedFrom":[makeQuery(id+"F15.opLoft","MID_CAP_EDGE",EDGE,{"disambiguationData":[OSD([subQ3,subQ5,subQ4]),TDD([makeQuery(id+"F6.imprint","INTERSECT",VERTEX,{"derivedFrom":[subQ3,subQ5]}),makeQuery(id+"F6.imprint","INTERSECT",VERTEX,{"derivedFrom":[subQ3,subQ4]}),makeQuery(id+"F6.imprint","IMPRINT",EDGE,{"derivedFrom":subQ3})])],"capPos":0.0}),makeQuery(id+"F17.opLoft","MID_CAP_EDGE",EDGE,{"disambiguationData":[OSD([subQ0,subQ1,subQ2]),TDD([makeQuery(id+"F10.imprint","INTERSECT",VERTEX,{"derivedFrom":[subQ0,subQ2]}),makeQuery(id+"F10.imprint","INTERSECT",VERTEX,{"derivedFrom":[subQ0,subQ1]}),makeQuery(id+"F10.imprint","IMPRINT",EDGE,{"derivedFrom":subQ0})])],"capPos":0.0})]});}
            var Q11;
            {var subQ0=sQuery(id+"F12.wireOp",EDGE,"E11.2");var subQ1=sQuery(id+"F12.wireOp",EDGE,"E11.1");var subQ2=sQuery(id+"F12.wireOp",EDGE,"E11.0");var subQ3=sQuery(id+"F2.wireOp",EDGE,"E1.1");var subQ4=sQuery(id+"F2.wireOp",EDGE,"E1.2");var subQ5=sQuery(id+"F2.wireOp",EDGE,"E1.0");var subQ6=makeQuery(id+"F16.boolean.opBoolean","MERGE",EDGE,{"derivedFrom":[makeQuery(id+"F15.opLoft","SWEPT_EDGE",EDGE,{"disambiguationData":[OSD([sQuery(id+"F6.wireOp",EDGE,"E5"),sQuery(id+"F6.wireOp",EDGE,"E8"),sQuery(id+"F8.wireOp",EDGE,"E9.0"),sQuery(id+"F8.wireOp",EDGE,"E9.2")])]}),makeQuery(id+"F16.opLoft","MID_CAP_EDGE",EDGE,{"disambiguationData":[OSD([subQ5,subQ3,subQ4]),TDD([makeQuery(id+"F2.imprint","INTERSECT",VERTEX,{"derivedFrom":[subQ5,subQ3]}),makeQuery(id+"F2.imprint","INTERSECT",VERTEX,{"derivedFrom":[subQ3,subQ4]}),makeQuery(id+"F2.imprint","IMPRINT",EDGE,{"derivedFrom":subQ3})])],"capPos":0.0})]});Q11=makeQuery(id+"F18.boolean.opBoolean","MERGE",EDGE,{"derivedFrom":[makeQuery(id+"F17.boolean.opBoolean","MERGE",EDGE,{"derivedFrom":[subQ6,makeQuery(id+"F17.opLoft","SWEPT_EDGE",EDGE,{"disambiguationData":[OSD([sQuery(id+"F0.wireOp",EDGE,"E0.1"),sQuery(id+"F0.wireOp",EDGE,"E0.2"),sQuery(id+"F10.wireOp",EDGE,"E10.0"),sQuery(id+"F10.wireOp",EDGE,"E10.1")])]})]}),makeQuery(id+"F17.boolean.opBoolean","SPLIT",EDGE,{"derivedFrom":subQ6}),makeQuery(id+"F18.opLoft","MID_CAP_EDGE",EDGE,{"disambiguationData":[OSD([subQ2,subQ1,subQ0]),TDD([makeQuery(id+"F12.imprint","INTERSECT",VERTEX,{"derivedFrom":[subQ2,subQ0]}),makeQuery(id+"F12.imprint","INTERSECT",VERTEX,{"derivedFrom":[subQ1,subQ0]}),makeQuery(id+"F12.imprint","IMPRINT",EDGE,{"derivedFrom":subQ0})])],"capPos":0.0})]});}
            var Q12;
            Q12=makeQuery(id+"F18.opLoft","CAP_FACE",FACE,{"disambiguationData":[OSD([makeQuery(id+"F12.imprint","IMPRINT",FACE,{"disambiguationData":[TD([[makeQuery(id+"F12.imprint","IMPRINT",EDGE,{"derivedFrom":sQuery(id+"F12.wireOp",EDGE,"E11.0")}),-1.0]])]})])],"isStart":true});
            var Q13;
            Q13=makeQuery(id+"F15.opLoft","CAP_FACE",FACE,{"disambiguationData":[OSD([makeQuery(id+"F8.imprint","IMPRINT",FACE,{"disambiguationData":[TD([[makeQuery(id+"F8.imprint","IMPRINT",EDGE,{"derivedFrom":sQuery(id+"F8.wireOp",EDGE,"E9.0")}),-1.0]])]})])],"isStart":true});
            var Q14;
            Q14=makeQuery(id+"F17.opLoft","CAP_FACE",FACE,{"disambiguationData":[OSD([makeQuery(id+"F10.imprint","IMPRINT",FACE,{"disambiguationData":[TD([[makeQuery(id+"F10.imprint","IMPRINT",EDGE,{"derivedFrom":sQuery(id+"F10.wireOp",EDGE,"E10.0")}),-1.0]])]})])],"isStart":true});
            var Q15;
            Q15=makeQuery(id+"F16.opLoft","CAP_FACE",FACE,{"disambiguationData":[OSD([makeQuery(id+"F14.imprint","IMPRINT",FACE,{"disambiguationData":[TD([[makeQuery(id+"F14.imprint","IMPRINT",EDGE,{"derivedFrom":sQuery(id+"F14.wireOp",EDGE,"E12.0")}),-1.0]])]})])],"isStart":true});
            var Q16;
            Q16=makeQuery(id+"F34.boolean.opBoolean","SPLIT",FACE,{"disambiguationData":[TD([makeQuery(id+"F34.opExtrude","SWEPT_FACE",FACE,{"disambiguationData":[OSD([sQuery(id+"F33.wireOp",EDGE,"E37.sketch_text.stroke-0")])]})])],"derivedFrom":makeQuery(id+"F18.opLoft","CAP_FACE",FACE,{"disambiguationData":[OSD([makeQuery(id+"F4.imprint","IMPRINT",FACE,{"disambiguationData":[TD([[makeQuery(id+"F4.imprint","IMPRINT",EDGE,{"derivedFrom":sQuery(id+"F4.wireOp",EDGE,"E2.0")}),-1.0]])]})])],"isStart":true})});
            var Q17;
            Q17=makeQuery(id+"F34.boolean.opBoolean","SPLIT",FACE,{"disambiguationData":[TD([makeQuery(id+"F34.opExtrude","SWEPT_FACE",FACE,{"disambiguationData":[OSD([sQuery(id+"F33.wireOp",EDGE,"E37.sketch_text.stroke-16")])]})])],"derivedFrom":makeQuery(id+"F18.opLoft","CAP_FACE",FACE,{"disambiguationData":[OSD([makeQuery(id+"F4.imprint","IMPRINT",FACE,{"disambiguationData":[TD([[makeQuery(id+"F4.imprint","IMPRINT",EDGE,{"derivedFrom":sQuery(id+"F4.wireOp",EDGE,"E2.0")}),-1.0]])]})])],"isStart":true})});
            var Q18;
            Q18=makeQuery(id+"F34.boolean.opBoolean","SPLIT",FACE,{"disambiguationData":[TD([makeQuery(id+"F34.opExtrude","SWEPT_FACE",FACE,{"disambiguationData":[OSD([sQuery(id+"F33.wireOp",EDGE,"E37.sketch_text.stroke-23")])]})])],"derivedFrom":makeQuery(id+"F18.opLoft","CAP_FACE",FACE,{"disambiguationData":[OSD([makeQuery(id+"F4.imprint","IMPRINT",FACE,{"disambiguationData":[TD([[makeQuery(id+"F4.imprint","IMPRINT",EDGE,{"derivedFrom":sQuery(id+"F4.wireOp",EDGE,"E2.0")}),-1.0]])]})])],"isStart":true})});
            var Q19;
            Q19=makeQuery(id+"F15.opLoft","CAP_FACE",FACE,{"disambiguationData":[OSD([makeQuery(id+"F6.imprint","IMPRINT",FACE,{"disambiguationData":[TD([[makeQuery(id+"F6.imprint","IMPRINT",EDGE,{"derivedFrom":sQuery(id+"F6.wireOp",EDGE,"E5")}),1.0]])]})])],"isStart":true});
            var Q20;
            Q20=makeQuery(id+"F30.boolean.opBoolean","SPLIT",FACE,{"disambiguationData":[TD([makeQuery(id+"F30.opExtrude","SWEPT_FACE",FACE,{"disambiguationData":[OSD([sQuery(id+"F29.wireOp",EDGE,"E29.sketch_text.stroke-0")])]})])],"derivedFrom":makeQuery(id+"F16.opLoft","CAP_FACE",FACE,{"disambiguationData":[OSD([makeQuery(id+"F2.imprint","IMPRINT",FACE,{"disambiguationData":[TD([[makeQuery(id+"F2.imprint","IMPRINT",EDGE,{"derivedFrom":sQuery(id+"F2.wireOp",EDGE,"E1.0")}),-1.0]])]})])],"isStart":true})});
            var Q21;
            Q21=makeQuery(id+"F30.boolean.opBoolean","COPY",EDGE,{"derivedFrom":makeQuery(id+"F30.opExtrude","CAP_EDGE",EDGE,{"disambiguationData":[OSD([sQuery(id+"F29.wireOp",EDGE,"E29.sketch_text.stroke-13")])],"isStart":true})});
            var Q22;
            Q22=makeQuery(id+"F30.boolean.opBoolean","COPY",EDGE,{"derivedFrom":makeQuery(id+"F30.opExtrude","CAP_EDGE",EDGE,{"disambiguationData":[OSD([sQuery(id+"F29.wireOp",EDGE,"E29.sketch_text.stroke-16")])],"isStart":true})});
            var Q23;
            Q23=makeQuery(id+"F30.boolean.opBoolean","COPY",EDGE,{"derivedFrom":makeQuery(id+"F30.opExtrude","CAP_EDGE",EDGE,{"disambiguationData":[OSD([sQuery(id+"F29.wireOp",EDGE,"E29.sketch_text.stroke-17")])],"isStart":true})});
            var Q24;
            Q24=makeQuery(id+"F28.boolean.opBoolean","SPLIT",FACE,{"disambiguationData":[TD([makeQuery(id+"F28.opExtrude","SWEPT_FACE",FACE,{"disambiguationData":[OSD([sQuery(id+"F27.wireOp",EDGE,"E28.sketch_text.stroke-17")])]})])],"derivedFrom":makeQuery(id+"F17.opLoft","CAP_FACE",FACE,{"disambiguationData":[OSD([makeQuery(id+"F0.imprint","IMPRINT",FACE,{"disambiguationData":[TD([[makeQuery(id+"F0.imprint","IMPRINT",EDGE,{"derivedFrom":sQuery(id+"F0.wireOp",EDGE,"E0.0")}),-1.0]])]})])],"isStart":true})});
            var Q25;
            Q25=makeQuery(id+"F28.boolean.opBoolean","SPLIT",FACE,{"disambiguationData":[TD([makeQuery(id+"F28.opExtrude","SWEPT_FACE",FACE,{"disambiguationData":[OSD([sQuery(id+"F27.wireOp",EDGE,"E28.sketch_text.stroke-0")])]})])],"derivedFrom":makeQuery(id+"F17.opLoft","CAP_FACE",FACE,{"disambiguationData":[OSD([makeQuery(id+"F0.imprint","IMPRINT",FACE,{"disambiguationData":[TD([[makeQuery(id+"F0.imprint","IMPRINT",EDGE,{"derivedFrom":sQuery(id+"F0.wireOp",EDGE,"E0.0")}),-1.0]])]})])],"isStart":true})});
            fillet(context, id + "F35", {"entities" : qUnion([Q0, Q1, Q2, Q3, Q4, Q5, Q6, Q7, Q8, Q9, Q10, Q11, Q12, Q13, Q14, Q15, Q16, Q17, Q18, Q19, Q20, Q21, Q22, Q23, Q24, Q25]), "radius" : .25 * mm, "tangentPropagation" : true, "allowEdgeOverflow" : false});
        }
    });
